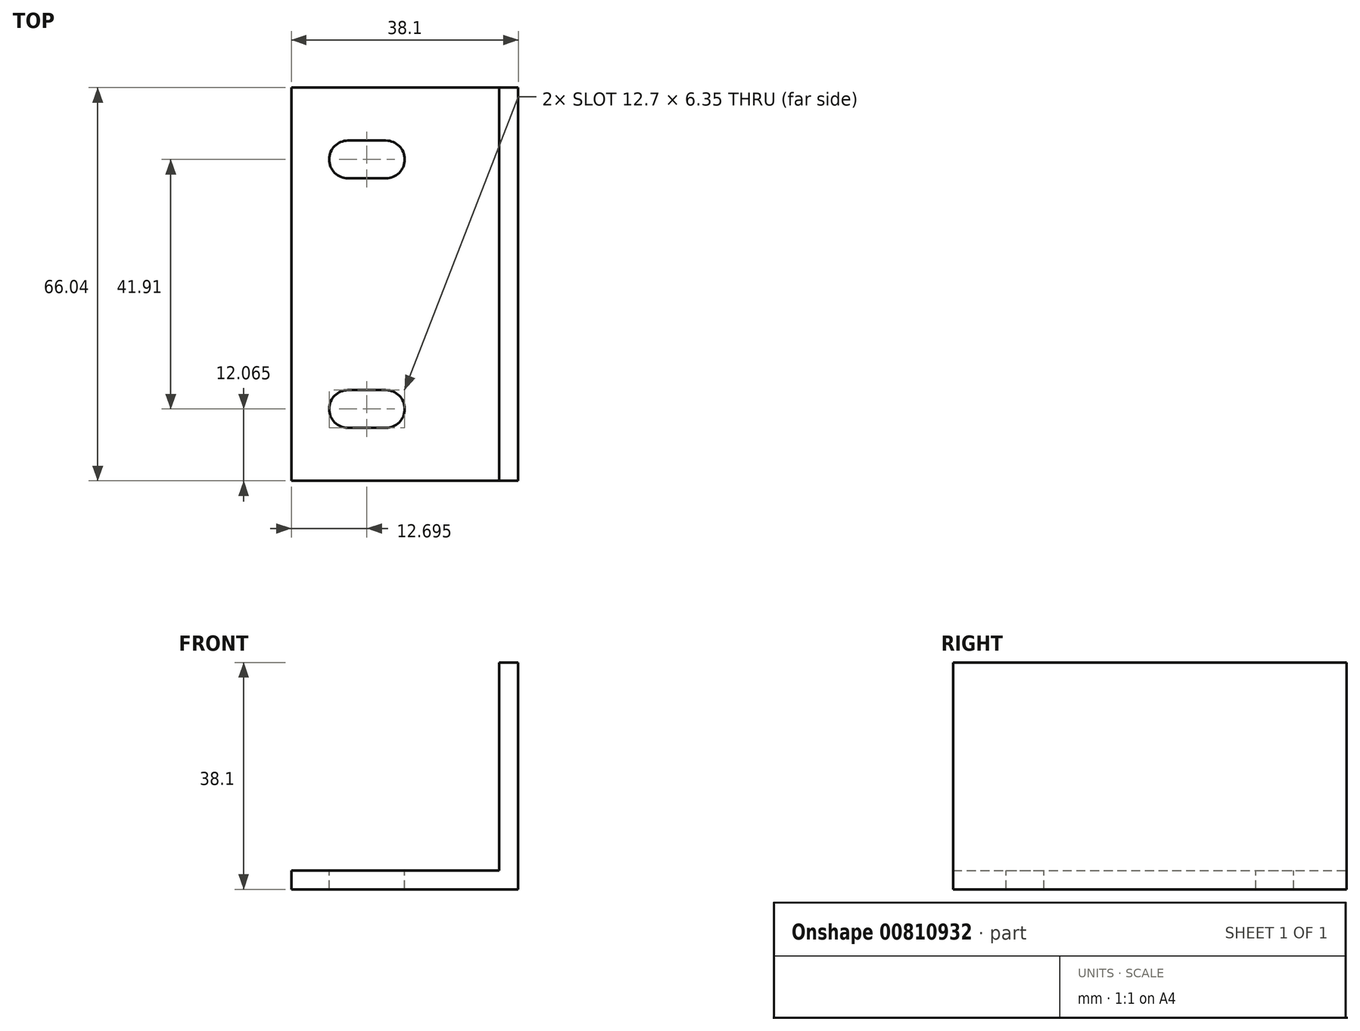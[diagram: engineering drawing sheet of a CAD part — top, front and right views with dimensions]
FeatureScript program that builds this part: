
annotation { "Feature Type Name" : "Feature", "Feature Type Description" : "" }
export const myFeature = defineFeature(function(context is Context, id is Id, definition is map)
    precondition{}
    {
        {
            var Q0;
            Q0=qCreatedBy(makeId("Front.planeOp"),FACE);
            var sketch = newSketch(context, id + "F0", { "sketchPlane" : qUnion([Q0])});
            skLineSegment(sketch, "E0.bottom", {"start": v(-34.93, -12.83) * mm, "end": v(0, -12.83) * mm});
            skLineSegment(sketch, "E0.top", {"start": v(-34.93, -16) * mm, "end": v(3.17, -16) * mm});
            skLineSegment(sketch, "E0.left", {"start": v(-34.93, -12.83) * mm, "end": v(-34.93, -16) * mm});
            skLineSegment(sketch, "E1.top", {"start": v(3.17, 22.1) * mm, "end": v(0, 22.1) * mm});
            skLineSegment(sketch, "E1.right", {"start": v(0, -12.83) * mm, "end": v(0, 22.1) * mm});
            skLineSegment(sketch, "E2", {"start": v(3.17, 22.1) * mm, "end": v(3.17, -16) * mm});
            skSolve(sketch);
        }
        {
            var Q0;
            Q0=makeQuery(id+"F0.imprint","IMPRINT",FACE,{"disambiguationData":[TD([[makeQuery(id+"F0.imprint","IMPRINT",EDGE,{"derivedFrom":sQuery(id+"F0.wireOp",EDGE,"E0.bottom")}),-1.0]])]});
            extrude(context, id + "F1", {"entities" : qUnion([Q0]), "endBound" : BoundingType.SYMMETRIC, "depth" : 66.04 * mm, "offsetDistance" : 25.4 * mm});
        }
        {
            var Q0;
            Q0=makeQuery(id+"F1.opExtrude","SWEPT_FACE",FACE,{"disambiguationData":[OSD([sQuery(id+"F0.wireOp",EDGE,"E0.bottom")])]});
            var sketch = newSketch(context, id + "F2", { "sketchPlane" : qUnion([Q0])});
            skLineSegment(sketch, "E3.bottom", {"start": v(-19.05, 17.78) * mm, "end": v(-25.4, 17.78) * mm});
            skLineSegment(sketch, "E3.top", {"start": v(-19.05, 24.13) * mm, "end": v(-25.4, 24.13) * mm});
            skLineSegment(sketch, "E3.left", {"start": v(-15.88, 20.96) * mm, "end": v(-15.88, 20.96) * mm});
            skLineSegment(sketch, "E3.right", {"start": v(-28.58, 20.96) * mm, "end": v(-28.58, 20.96) * mm});
            skPoint(sketch, "E3.middle", {"position": v(-22.23, 20.96) * mm});
            skPoint(sketch, "E4.visualSharp", {"position": v(-15.88, 24.13) * mm});
            skArc(sketch, "E4.filletArc", {"start": v(-15.88, 20.96) * mm, "mid": v(-16.8, 23.2) * mm, "end": v(-19.05, 24.13) * mm});
            skPoint(sketch, "E5.visualSharp", {"position": v(-15.88, 17.78) * mm});
            skArc(sketch, "E5.filletArc", {"start": v(-19.05, 17.78) * mm, "mid": v(-16.8, 18.7) * mm, "end": v(-15.87, 20.96) * mm});
            skPoint(sketch, "E6.visualSharp", {"position": v(-28.58, 24.13) * mm});
            skArc(sketch, "E6.filletArc", {"start": v(-25.4, 24.13) * mm, "mid": v(-27.65, 23.2) * mm, "end": v(-28.58, 20.96) * mm});
            skPoint(sketch, "E7.visualSharp", {"position": v(-28.58, 17.78) * mm});
            skArc(sketch, "E7.filletArc", {"start": v(-28.58, 20.96) * mm, "mid": v(-27.65, 18.7) * mm, "end": v(-25.4, 17.78) * mm});
            skArc(sketch, "E8.MirrorCS", {"start": v(-28.58, -20.96) * mm, "mid": v(-27.65, -18.7) * mm, "end": v(-25.4, -17.78) * mm});
            skArc(sketch, "E9.MirrorCS", {"start": v(-25.4, -24.13) * mm, "mid": v(-27.65, -23.2) * mm, "end": v(-28.58, -20.96) * mm});
            skArc(sketch, "E10.MirrorCS", {"start": v(-19.05, -17.78) * mm, "mid": v(-16.8, -18.7) * mm, "end": v(-15.87, -20.96) * mm});
            skArc(sketch, "E11.MirrorCS", {"start": v(-15.88, -20.96) * mm, "mid": v(-16.8, -23.2) * mm, "end": v(-19.05, -24.13) * mm});
            skPoint(sketch, "E12.MirrorP", {"position": v(-22.23, -20.96) * mm});
            skPoint(sketch, "E13.MirrorP", {"position": v(-15.88, -24.13) * mm});
            skPoint(sketch, "E14.MirrorP", {"position": v(-28.58, -17.78) * mm});
            skPoint(sketch, "E15.MirrorP", {"position": v(-15.88, -17.78) * mm});
            skPoint(sketch, "E16.MirrorP", {"position": v(-28.58, -24.13) * mm});
            skLineSegment(sketch, "E17.MirrorCS", {"start": v(-19.05, -24.13) * mm, "end": v(-25.4, -24.13) * mm});
            skLineSegment(sketch, "E18.MirrorCS", {"start": v(-19.05, -17.78) * mm, "end": v(-25.4, -17.78) * mm});
            skSolve(sketch);
        }
        {
            var Q0;
            Q0 = qSketchRegion(id + "F2", true);
            extrude(context, id + "F3", {"entities" : qUnion([Q0]), "operationType" : NewBodyOperationType.REMOVE, "endBound" : BoundingType.UP_TO_NEXT, "oppositeDirection" : true, "depth" : 25.4 * mm, "offsetDistance" : 25.4 * mm});
        }
    });
